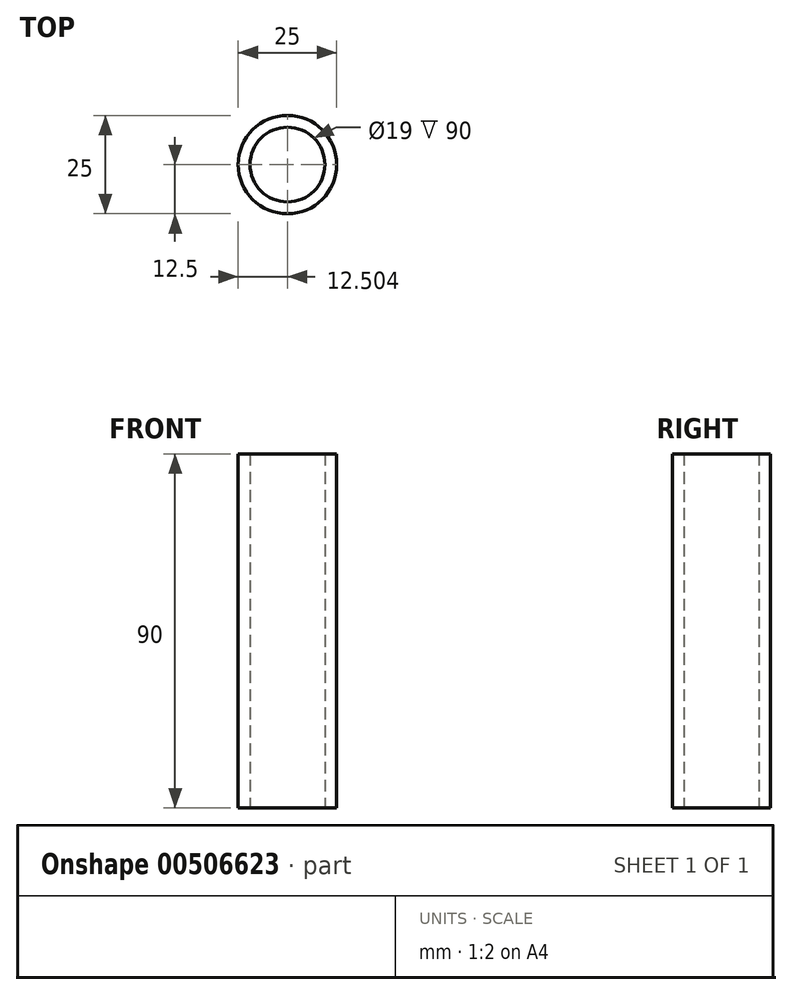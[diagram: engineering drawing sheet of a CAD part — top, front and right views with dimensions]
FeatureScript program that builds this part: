
annotation { "Feature Type Name" : "Feature", "Feature Type Description" : "" }
export const myFeature = defineFeature(function(context is Context, id is Id, definition is map)
    precondition{}
    {
        {
            var Q0;
            Q0=qCreatedBy(makeId("Top.planeOp"),FACE);
            var sketch = newSketch(context, id + "F0", { "sketchPlane" : qUnion([Q0])});
            skCircle(sketch, "E0", {"center": v(4.87, 9.95) * mm, "radius": 12.5 * mm});
            skCircle(sketch, "E1", {"center": v(4.87, 9.95) * mm, "radius": 9.5 * mm});
            skSolve(sketch);
        }
        {
            var Q0;
            Q0=qSketchRegion(id+"F0",true);
            extrude(context, id + "F1", {"entities" : qUnion([Q0]), "depth" : 90 * mm});
        }
    });
